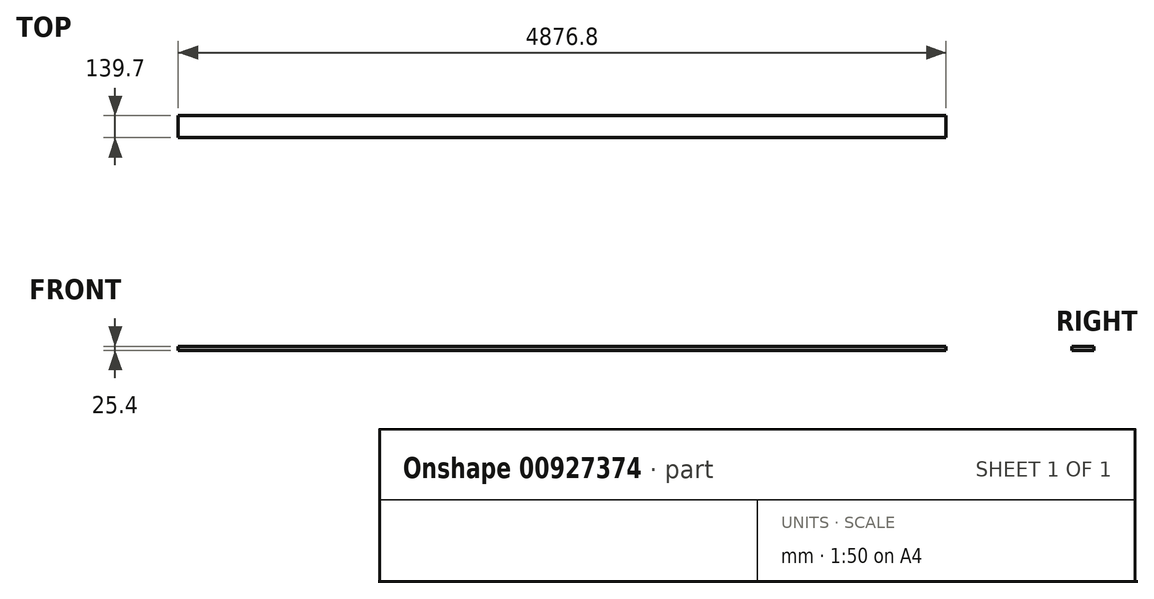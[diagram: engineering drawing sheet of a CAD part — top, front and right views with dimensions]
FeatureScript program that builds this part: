
annotation { "Feature Type Name" : "Feature", "Feature Type Description" : "" }
export const myFeature = defineFeature(function(context is Context, id is Id, definition is map)
    precondition{}
    {
        {
            var Q0;
            Q0=qCreatedBy(makeId("Top.planeOp"),FACE);
            var sketch = newSketch(context, id + "F0", { "sketchPlane" : qUnion([Q0])});
            skLineSegment(sketch, "E0.bottom", {"start": v(-2438.4, 69.85) * mm, "end": v(2438.4, 69.85) * mm});
            skLineSegment(sketch, "E0.top", {"start": v(-2438.4, -69.85) * mm, "end": v(2438.4, -69.85) * mm});
            skLineSegment(sketch, "E0.left", {"start": v(-2438.4, 69.85) * mm, "end": v(-2438.4, -69.85) * mm});
            skLineSegment(sketch, "E0.right", {"start": v(2438.4, 69.85) * mm, "end": v(2438.4, -69.85) * mm});
            skLineSegment(sketch, "E1", {"start": v(2438.4, 69.85) * mm, "end": v(-2438.4, -69.85) * mm, "construction": true});
            skSolve(sketch);
        }
        {
            var Q0;
            Q0=makeQuery(id+"F0.imprint","IMPRINT",FACE,{"disambiguationData":[TD([[makeQuery(id+"F0.imprint","IMPRINT",EDGE,{"derivedFrom":sQuery(id+"F0.wireOp",EDGE,"E0.bottom")}),-1.0]])]});
            extrude(context, id + "F1", {"entities" : qUnion([Q0]), "depth" : 25.4 * mm, "offsetDistance" : 25.4 * mm});
        }
    });
